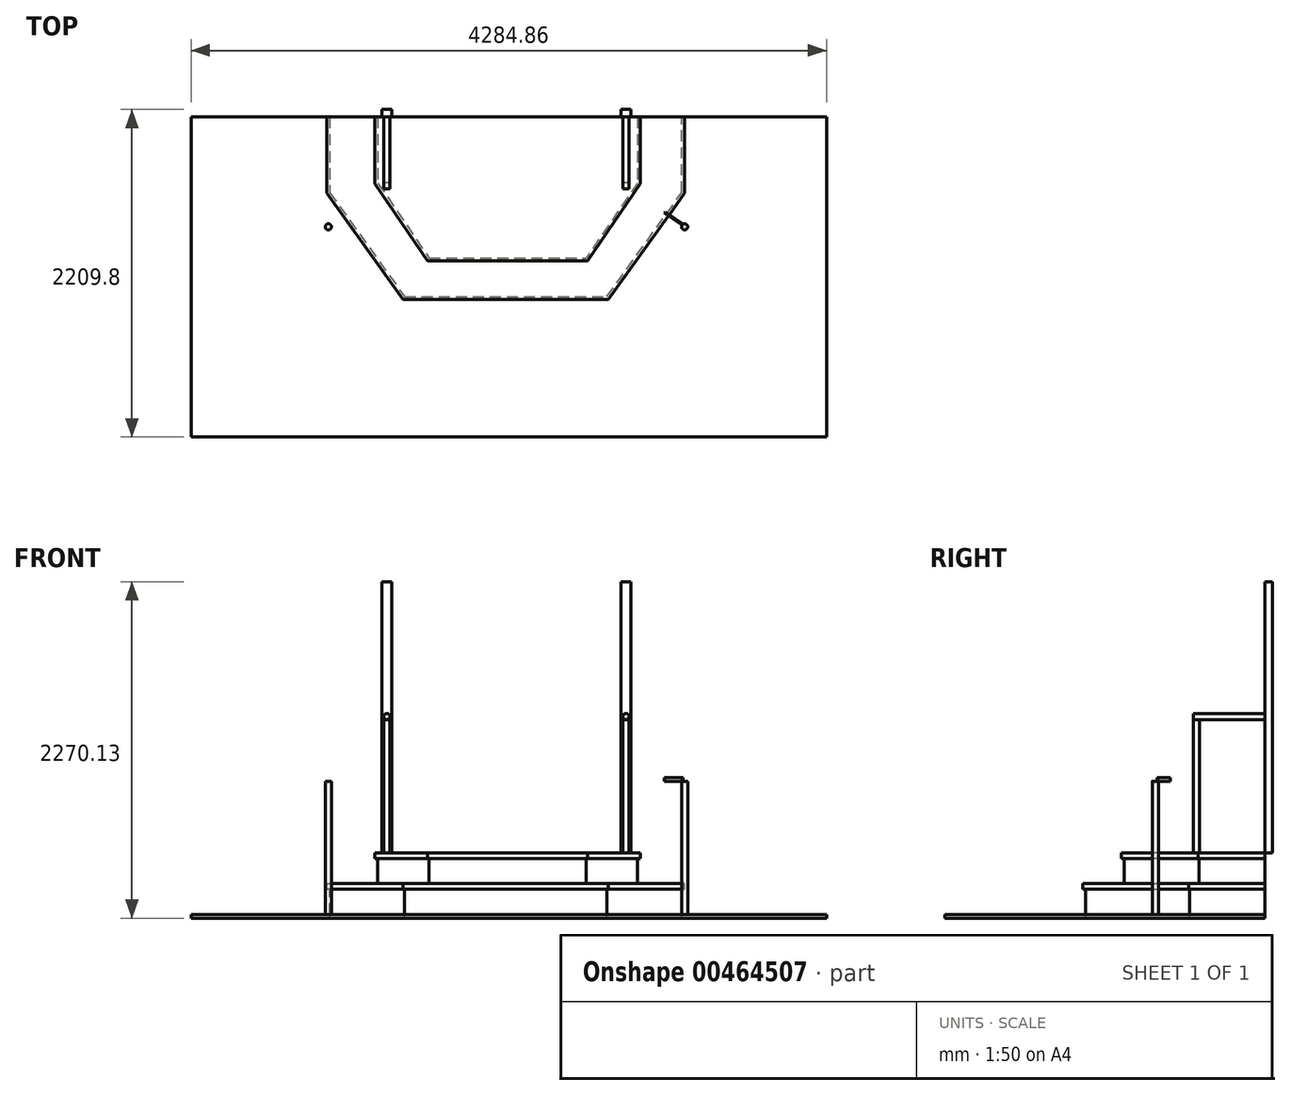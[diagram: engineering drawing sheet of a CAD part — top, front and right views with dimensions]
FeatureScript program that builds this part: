
annotation { "Feature Type Name" : "Feature", "Feature Type Description" : "" }
export const myFeature = defineFeature(function(context is Context, id is Id, definition is map)
    precondition{}
    {
        {
            var Q0;
            Q0=qCreatedBy(makeId("Top.planeOp"),FACE);
            var sketch = newSketch(context, id + "F0", { "sketchPlane" : qUnion([Q0])});
            skLineSegment(sketch, "E0", {"start": v(0, 0) * mm, "end": v(-895.35, 0) * mm});
            skLineSegment(sketch, "E1", {"start": v(-895.35, 0) * mm, "end": v(-895.35, -450.85) * mm});
            skLineSegment(sketch, "E2", {"start": v(-895.35, -450.85) * mm, "end": v(-539.75, -969.26) * mm});
            skLineSegment(sketch, "E3", {"start": v(-539.75, -969.26) * mm, "end": v(0, -969.26) * mm});
            skLineSegment(sketch, "E4", {"start": v(0, -969.26) * mm, "end": v(0, 0) * mm});
            skLineSegment(sketch, "E5.MirrorCS", {"start": v(0, 0) * mm, "end": v(895.35, 0) * mm});
            skLineSegment(sketch, "E6.MirrorCS", {"start": v(895.35, 0) * mm, "end": v(895.35, -450.85) * mm});
            skLineSegment(sketch, "E7.MirrorCS", {"start": v(895.35, -450.85) * mm, "end": v(539.75, -969.26) * mm});
            skLineSegment(sketch, "E8.MirrorCS", {"start": v(539.75, -969.26) * mm, "end": v(0, -969.26) * mm});
            skSolve(sketch);
        }
        {
            var Q0;
            Q0=makeQuery(id+"F0.imprint","IMPRINT",FACE,{"disambiguationData":[TD([[makeQuery(id+"F0.imprint","IMPRINT",EDGE,{"derivedFrom":sQuery(id+"F0.wireOp",EDGE,"E0")}),1.0]])]});
            var Q1;
            Q1=makeQuery(id+"F0.imprint","IMPRINT",FACE,{"disambiguationData":[TD([[makeQuery(id+"F0.imprint","IMPRINT",EDGE,{"derivedFrom":sQuery(id+"F0.wireOp",EDGE,"E4")}),-1.0]])]});
            extrude(context, id + "F1", {"entities" : qUnion([Q0, Q1]), "oppositeDirection" : true, "depth" : 38.1 * mm});
        }
        {
            var Q0;
            Q0=makeQuery(id+"F1.opExtrude","CAP_FACE",FACE,{"disambiguationData":[OSD([sQuery(id+"F0.wireOp",EDGE,"E0"),sQuery(id+"F0.wireOp",EDGE,"E1"),sQuery(id+"F0.wireOp",EDGE,"E2"),sQuery(id+"F0.wireOp",EDGE,"E3"),sQuery(id+"F0.wireOp",EDGE,"E5.MirrorCS"),sQuery(id+"F0.wireOp",EDGE,"E6.MirrorCS"),sQuery(id+"F0.wireOp",EDGE,"E7.MirrorCS"),sQuery(id+"F0.wireOp",EDGE,"E8.MirrorCS")])],"isStart":false});
            var sketch = newSketch(context, id + "F2", { "sketchPlane" : qUnion([Q0])});
            skLineSegment(sketch, "E9.0", {"start": v(876.3, 0) * mm, "end": v(876.3, 444.94) * mm});
            skLineSegment(sketch, "E9.1", {"start": v(-876.3, 0) * mm, "end": v(-876.3, 444.94) * mm});
            skLineSegment(sketch, "E9.2", {"start": v(-876.3, 444.94) * mm, "end": v(-529.72, 950.21) * mm});
            skLineSegment(sketch, "E9.3", {"start": v(-529.72, 950.21) * mm, "end": v(529.72, 950.21) * mm});
            skLineSegment(sketch, "E9.4", {"start": v(876.3, 444.94) * mm, "end": v(529.72, 950.21) * mm});
            skSolve(sketch);
        }
        {
            var Q0;
            {var subQ1=sQuery(id+"F2.wireOp",EDGE,"E9.0");Q0=makeQuery(id+"F2.imprint","IMPRINT",FACE,{"disambiguationData":[TD([[makeQuery(id+"F2.imprint","IMPRINT",EDGE,{"derivedFrom":subQ1}),1.0]])]});}
            extrude(context, id + "F3", {"entities" : qUnion([Q0]), "operationType" : NewBodyOperationType.ADD, "depth" : 168.27 * mm});
        }
        {
            var Q0;
            Q0=makeQuery(id+"F3.opExtrude","CAP_FACE",FACE,{"disambiguationData":[OSD([sQuery(id+"F0.wireOp",EDGE,"E0"),sQuery(id+"F0.wireOp",EDGE,"E5.MirrorCS"),sQuery(id+"F2.wireOp",EDGE,"E9.0"),sQuery(id+"F2.wireOp",EDGE,"E9.1"),sQuery(id+"F2.wireOp",EDGE,"E9.2"),sQuery(id+"F2.wireOp",EDGE,"E9.3"),sQuery(id+"F2.wireOp",EDGE,"E9.4")])],"isStart":false});
            var sketch = newSketch(context, id + "F4", { "sketchPlane" : qUnion([Q0])});
            skLineSegment(sketch, "E10", {"start": v(0, 0) * mm, "end": v(-1219.2, 0) * mm});
            skLineSegment(sketch, "E11", {"start": v(0, 0) * mm, "end": v(1193.8, 0) * mm});
            skLineSegment(sketch, "E12", {"start": v(-1219.2, 0) * mm, "end": v(-1219.2, 514.35) * mm});
            skLineSegment(sketch, "E13", {"start": v(-1219.2, 514.35) * mm, "end": v(-704.85, 1231.65) * mm});
            skLineSegment(sketch, "E14", {"start": v(-704.85, 1231.65) * mm, "end": v(679.45, 1231.65) * mm});
            skLineSegment(sketch, "E15", {"start": v(679.45, 1231.65) * mm, "end": v(1193.8, 514.35) * mm});
            skLineSegment(sketch, "E16", {"start": v(1193.8, 514.35) * mm, "end": v(1193.8, 0) * mm});
            skSolve(sketch);
        }
        {
            var Q0;
            {var subQ4=sQuery(id+"F4.wireOp",EDGE,"E12");Q0=makeQuery(id+"F4.imprint","IMPRINT",FACE,{"disambiguationData":[TD([[makeQuery(id+"F4.imprint","IMPRINT",EDGE,{"derivedFrom":subQ4}),-1.0]])]});}
            var Q1;
            {var subQ0=makeQuery(id+"F3.opExtrude","CAP_EDGE",EDGE,{"disambiguationData":[OSD([sQuery(id+"F2.wireOp",EDGE,"E9.0")])],"isStart":false});Q1=makeQuery(id+"F4.imprint","IMPRINT",FACE,{"disambiguationData":[TD([[makeQuery(id+"F4.imprint","IMPRINT",EDGE,{"derivedFrom":subQ0}),1.0]])]});}
            extrude(context, id + "F5", {"entities" : qUnion([Q0, Q1]), "operationType" : NewBodyOperationType.ADD, "depth" : 38.1 * mm});
        }
        {
            var Q0;
            Q0=makeQuery(id+"F5.opExtrude","CAP_FACE",FACE,{"disambiguationData":[OSD([sQuery(id+"F4.wireOp",EDGE,"E10"),sQuery(id+"F4.wireOp",EDGE,"E11"),sQuery(id+"F4.wireOp",EDGE,"E12"),sQuery(id+"F4.wireOp",EDGE,"E13"),sQuery(id+"F4.wireOp",EDGE,"E14"),sQuery(id+"F4.wireOp",EDGE,"E15"),sQuery(id+"F4.wireOp",EDGE,"E16")])],"isStart":false});
            var sketch = newSketch(context, id + "F6", { "sketchPlane" : qUnion([Q0])});
            skLineSegment(sketch, "E17.0", {"start": v(1174.75, 508.23) * mm, "end": v(1174.75, 0) * mm});
            skLineSegment(sketch, "E17.1", {"start": v(-1200.15, 0) * mm, "end": v(-1200.15, 508.23) * mm});
            skLineSegment(sketch, "E17.2", {"start": v(-1200.15, 508.23) * mm, "end": v(-695.07, 1212.6) * mm});
            skLineSegment(sketch, "E17.3", {"start": v(-695.07, 1212.6) * mm, "end": v(669.67, 1212.6) * mm});
            skLineSegment(sketch, "E17.4", {"start": v(669.67, 1212.6) * mm, "end": v(1174.75, 508.23) * mm});
            skSolve(sketch);
        }
        {
            var Q0;
            {var subQ1=sQuery(id+"F6.wireOp",EDGE,"E17.0");Q0=makeQuery(id+"F6.imprint","IMPRINT",FACE,{"disambiguationData":[TD([[makeQuery(id+"F6.imprint","IMPRINT",EDGE,{"derivedFrom":subQ1}),-1.0]])]});}
            extrude(context, id + "F7", {"entities" : qUnion([Q0]), "operationType" : NewBodyOperationType.ADD, "depth" : 171.45 * mm});
        }
        {
            var Q0;
            Q0=makeQuery(id+"F7.opExtrude","CAP_FACE",FACE,{"disambiguationData":[OSD([sQuery(id+"F4.wireOp",EDGE,"E10"),sQuery(id+"F4.wireOp",EDGE,"E11"),sQuery(id+"F6.wireOp",EDGE,"E17.0"),sQuery(id+"F6.wireOp",EDGE,"E17.1"),sQuery(id+"F6.wireOp",EDGE,"E17.2"),sQuery(id+"F6.wireOp",EDGE,"E17.3"),sQuery(id+"F6.wireOp",EDGE,"E17.4")])],"isStart":false});
            var sketch = newSketch(context, id + "F8", { "sketchPlane" : qUnion([Q0])});
            skLineSegment(sketch, "E18.bottom", {"start": v(0, 0) * mm, "end": v(-2134.43, 0) * mm});
            skLineSegment(sketch, "E18.top", {"start": v(0, 2159) * mm, "end": v(-2134.43, 2159) * mm});
            skLineSegment(sketch, "E18.left", {"start": v(0, 0) * mm, "end": v(0, 2159) * mm});
            skLineSegment(sketch, "E18.right", {"start": v(-2134.43, 0) * mm, "end": v(-2134.43, 2159) * mm});
            skLineSegment(sketch, "E19.bottom", {"start": v(0, 0) * mm, "end": v(2150.43, 0) * mm});
            skLineSegment(sketch, "E19.top", {"start": v(0, 2159) * mm, "end": v(2150.43, 2159) * mm});
            skLineSegment(sketch, "E19.right", {"start": v(2150.43, 0) * mm, "end": v(2150.43, 2159) * mm});
            skSolve(sketch);
        }
        {
            var Q0;
            {var subQ1=sQuery(id+"F8.wireOp",EDGE,"E18.top");Q0=makeQuery(id+"F8.imprint","IMPRINT",FACE,{"disambiguationData":[TD([[makeQuery(id+"F8.imprint","IMPRINT",EDGE,{"derivedFrom":subQ1}),1.0]])]});}
            var Q1;
            {var subQ2=sQuery(id+"F8.wireOp",EDGE,"E19.top");Q1=makeQuery(id+"F8.imprint","IMPRINT",FACE,{"disambiguationData":[TD([[makeQuery(id+"F8.imprint","IMPRINT",EDGE,{"derivedFrom":subQ2}),-1.0]])]});}
            extrude(context, id + "F9", {"entities" : qUnion([Q0, Q1]), "depth" : 25.4 * mm});
        }
        {
            var Q0;
            {var subQ0=sQuery(id+"F4.wireOp",EDGE,"E11");var subQ1=sQuery(id+"F4.wireOp",EDGE,"E10");var subQ2=sQuery(id+"F0.wireOp",EDGE,"E5.MirrorCS");var subQ3=sQuery(id+"F0.wireOp",EDGE,"E0");Q0=makeQuery(id+"F7.boolean.opBoolean","MERGE",FACE,{"derivedFrom":[makeQuery(id+"F5.boolean.opBoolean","MERGE",FACE,{"derivedFrom":[makeQuery(id+"F3.boolean.opBoolean","MERGE",FACE,{"derivedFrom":[makeQuery(id+"F1.opExtrude","SWEPT_FACE",FACE,{"disambiguationData":[OSD([subQ3,subQ2])]}),makeQuery(id+"F3.opExtrude","SWEPT_FACE",FACE,{"disambiguationData":[OSD([subQ3,subQ2])]})]}),makeQuery(id+"F5.opExtrude","SWEPT_FACE",FACE,{"disambiguationData":[OSD([subQ1,subQ0])]})]}),makeQuery(id+"F7.opExtrude","SWEPT_FACE",FACE,{"disambiguationData":[OSD([subQ1,subQ0])]})]});}
            var sketch = newSketch(context, id + "F10", { "sketchPlane" : qUnion([Q0])});
            skLineSegment(sketch, "E20.bottom", {"start": v(847.72, 0) * mm, "end": v(781.05, 0) * mm});
            skLineSegment(sketch, "E20.top", {"start": v(847.72, 1828.8) * mm, "end": v(781.05, 1828.8) * mm});
            skLineSegment(sketch, "E20.left", {"start": v(847.72, 0) * mm, "end": v(847.72, 1828.8) * mm});
            skLineSegment(sketch, "E20.right", {"start": v(781.05, 0) * mm, "end": v(781.05, 1828.8) * mm});
            skLineSegment(sketch, "E21.bottom", {"start": v(-765.17, 0) * mm, "end": v(-831.85, 0) * mm});
            skLineSegment(sketch, "E21.top", {"start": v(-765.17, 1828.8) * mm, "end": v(-831.85, 1828.8) * mm});
            skLineSegment(sketch, "E21.left", {"start": v(-765.17, 0) * mm, "end": v(-765.17, 1828.8) * mm});
            skLineSegment(sketch, "E21.right", {"start": v(-831.85, 0) * mm, "end": v(-831.85, 1828.8) * mm});
            skSolve(sketch);
        }
        {
            var Q0;
            Q0=makeQuery(id+"F10.imprint","IMPRINT",FACE,{"disambiguationData":[TD([[makeQuery(id+"F10.imprint","IMPRINT",EDGE,{"derivedFrom":sQuery(id+"F10.wireOp",EDGE,"E20.bottom")}),1.0]])]});
            var Q1;
            Q1=makeQuery(id+"F10.imprint","IMPRINT",FACE,{"disambiguationData":[TD([[makeQuery(id+"F10.imprint","IMPRINT",EDGE,{"derivedFrom":sQuery(id+"F10.wireOp",EDGE,"E21.bottom")}),1.0]])]});
            extrude(context, id + "F11", {"entities" : qUnion([Q0, Q1]), "depth" : 50.8 * mm});
        }
        {
            var Q0;
            Q0=makeQuery(id+"F1.opExtrude","CAP_FACE",FACE,{"disambiguationData":[OSD([sQuery(id+"F0.wireOp",EDGE,"E0"),sQuery(id+"F0.wireOp",EDGE,"E1"),sQuery(id+"F0.wireOp",EDGE,"E2"),sQuery(id+"F0.wireOp",EDGE,"E3"),sQuery(id+"F0.wireOp",EDGE,"E5.MirrorCS"),sQuery(id+"F0.wireOp",EDGE,"E6.MirrorCS"),sQuery(id+"F0.wireOp",EDGE,"E7.MirrorCS"),sQuery(id+"F0.wireOp",EDGE,"E8.MirrorCS")])],"isStart":true});
            var sketch = newSketch(context, id + "F12", { "sketchPlane" : qUnion([Q0])});
            skPoint(sketch, "E22.0", {"position": v(831.85, 0) * mm});
            skPoint(sketch, "E23.0", {"position": v(765.17, 0) * mm});
            skPoint(sketch, "E24.0", {"position": v(-847.72, 0) * mm});
            skPoint(sketch, "E25.0", {"position": v(-781.05, 0) * mm});
            skCircle(sketch, "E26", {"center": v(798.51, -463.55) * mm, "radius": 20.64 * mm});
            skLineSegment(sketch, "E27", {"start": v(798.51, 0) * mm, "end": v(798.51, -463.55) * mm});
            skLineSegment(sketch, "E28", {"start": v(798.51, -463.55) * mm, "end": v(1218.12, -751.38) * mm});
            skCircle(sketch, "E29", {"center": v(-814.37, -463.55) * mm, "radius": 20.64 * mm});
            skSolve(sketch);
        }
        {
            var Q0;
            {var subQ0=sQuery(id+"F12.wireOp",EDGE,"E27");var subQ1=sQuery(id+"F12.wireOp",EDGE,"E26");var subQ2=makeQuery(id+"F12.imprint","INTERSECT",VERTEX,{"derivedFrom":[subQ1,subQ0]});Q0=makeQuery(id+"F12.imprint","IMPRINT",FACE,{"disambiguationData":[TD([[makeQuery(id+"F12.imprint","IMPRINT",EDGE,{"disambiguationData":[TD([[subQ2,-1.0]])],"derivedFrom":subQ1}),1.0]])]});}
            var Q1;
            {var subQ0=sQuery(id+"F12.wireOp",EDGE,"E27");var subQ1=sQuery(id+"F12.wireOp",EDGE,"E26");var subQ2=makeQuery(id+"F12.imprint","INTERSECT",VERTEX,{"derivedFrom":[subQ1,subQ0]});Q1=makeQuery(id+"F12.imprint","IMPRINT",FACE,{"disambiguationData":[TD([[makeQuery(id+"F12.imprint","IMPRINT",EDGE,{"disambiguationData":[TD([[subQ2,1.0]])],"derivedFrom":subQ1}),1.0]])]});}
            var Q2;
            Q2=makeQuery(id+"F12.imprint","IMPRINT",FACE,{"disambiguationData":[TD([[makeQuery(id+"F12.imprint","IMPRINT",EDGE,{"derivedFrom":sQuery(id+"F12.wireOp",EDGE,"E29")}),1.0]])]});
            extrude(context, id + "F13", {"entities" : qUnion([Q0, Q1, Q2]), "operationType" : NewBodyOperationType.ADD, "depth" : 898.52 * mm});
        }
        {
            var Q0;
            Q0=makeQuery(id+"F11.opExtrude","CAP_FACE",FACE,{"disambiguationData":[OSD([sQuery(id+"F10.wireOp",EDGE,"E21.bottom"),sQuery(id+"F10.wireOp",EDGE,"E21.top"),sQuery(id+"F10.wireOp",EDGE,"E21.left"),sQuery(id+"F10.wireOp",EDGE,"E21.right")])],"isStart":true});
            var sketch = newSketch(context, id + "F14", { "sketchPlane" : qUnion([Q0])});
            skCircle(sketch, "E30", {"center": v(798.51, 919.16) * mm, "radius": 20.64 * mm});
            skSolve(sketch);
        }
        {
            var Q0;
            {var subQ0=sQuery(id+"F4.wireOp",EDGE,"E11");var subQ1=sQuery(id+"F4.wireOp",EDGE,"E10");var subQ2=sQuery(id+"F0.wireOp",EDGE,"E5.MirrorCS");var subQ3=sQuery(id+"F0.wireOp",EDGE,"E0");Q0=makeQuery(id+"F7.boolean.opBoolean","MERGE",FACE,{"derivedFrom":[makeQuery(id+"F5.boolean.opBoolean","MERGE",FACE,{"derivedFrom":[makeQuery(id+"F3.boolean.opBoolean","MERGE",FACE,{"derivedFrom":[makeQuery(id+"F1.opExtrude","SWEPT_FACE",FACE,{"disambiguationData":[OSD([subQ3,subQ2])]}),makeQuery(id+"F3.opExtrude","SWEPT_FACE",FACE,{"disambiguationData":[OSD([subQ3,subQ2])]})]}),makeQuery(id+"F5.opExtrude","SWEPT_FACE",FACE,{"disambiguationData":[OSD([subQ1,subQ0])]})]}),makeQuery(id+"F7.opExtrude","SWEPT_FACE",FACE,{"disambiguationData":[OSD([subQ1,subQ0])]})]});}
            var sketch = newSketch(context, id + "F15", { "sketchPlane" : qUnion([Q0])});
            skLineSegment(sketch, "E31", {"start": v(-895.35, 0) * mm, "end": v(-1518, -430.56) * mm});
            skSolve(sketch);
        }
        {
            var Q0;
            Q0=makeQuery(id+"F1.opExtrude","CAP_FACE",FACE,{"disambiguationData":[OSD([sQuery(id+"F0.wireOp",EDGE,"E0"),sQuery(id+"F0.wireOp",EDGE,"E1"),sQuery(id+"F0.wireOp",EDGE,"E2"),sQuery(id+"F0.wireOp",EDGE,"E3"),sQuery(id+"F0.wireOp",EDGE,"E5.MirrorCS"),sQuery(id+"F0.wireOp",EDGE,"E6.MirrorCS"),sQuery(id+"F0.wireOp",EDGE,"E7.MirrorCS"),sQuery(id+"F0.wireOp",EDGE,"E8.MirrorCS")])],"isStart":true});
            cPlane(context, id + "F16", {"entities" : qUnion([Q0]), "cplaneType" : CPlaneType.OFFSET, "offset" : 939.8 * mm, "width" : 152.4 * mm, "height" : 152.4 * mm});
        }
        {
            var Q0;
            Q0=qCreatedBy(id+"F16.planeOp",FACE);
            var sketch = newSketch(context, id + "F17", { "sketchPlane" : qUnion([Q0])});
            skLineSegment(sketch, "E32.0", {"start": v(819.15, -484.19) * mm, "end": v(777.88, -484.19) * mm});
            skLineSegment(sketch, "E33", {"start": v(819.15, 0) * mm, "end": v(819.15, -484.19) * mm});
            skLineSegment(sketch, "E34", {"start": v(777.88, -484.19) * mm, "end": v(819.15, -425.24) * mm});
            skLineSegment(sketch, "E35.0", {"start": v(895.35, -450.85) * mm, "end": v(539.75, -969.26) * mm});
            skLineSegment(sketch, "E35.1", {"start": v(895.35, 0) * mm, "end": v(895.35, -450.85) * mm});
            skSolve(sketch);
        }
        {
            var Q0;
            Q0=makeQuery(id+"F9.opExtrude","CAP_FACE",FACE,{"disambiguationData":[OSD([sQuery(id+"F6.wireOp",EDGE,"E17.0"),sQuery(id+"F6.wireOp",EDGE,"E17.1"),sQuery(id+"F6.wireOp",EDGE,"E17.2"),sQuery(id+"F6.wireOp",EDGE,"E17.3"),sQuery(id+"F6.wireOp",EDGE,"E17.4"),sQuery(id+"F8.wireOp",EDGE,"E18.bottom"),sQuery(id+"F8.wireOp",EDGE,"E18.top"),sQuery(id+"F8.wireOp",EDGE,"E18.right"),sQuery(id+"F8.wireOp",EDGE,"E19.bottom"),sQuery(id+"F8.wireOp",EDGE,"E19.top"),sQuery(id+"F8.wireOp",EDGE,"E19.right")])],"isStart":true});
            var sketch = newSketch(context, id + "F18", { "sketchPlane" : qUnion([Q0])});
            skLineSegment(sketch, "E36", {"start": v(819.15, 0) * mm, "end": v(819.15, -425.24) * mm});
            skLineSegment(sketch, "E37.0", {"start": v(777.88, -484.19) * mm, "end": v(819.15, -425.24) * mm});
            skCircle(sketch, "E38.0", {"center": v(798.51, -463.55) * mm, "radius": 20.64 * mm});
            skLineSegment(sketch, "E39.0", {"start": v(1193.8, -514.35) * mm, "end": v(1193.8, 0) * mm});
            skLineSegment(sketch, "E40.0", {"start": v(679.45, -1231.65) * mm, "end": v(1193.8, -514.35) * mm});
            skLineSegment(sketch, "E41.0", {"start": v(895.35, 0) * mm, "end": v(895.35, -450.85) * mm});
            skLineSegment(sketch, "E42.0", {"start": v(895.35, -450.85) * mm, "end": v(539.75, -969.26) * mm});
            skLineSegment(sketch, "E43", {"start": v(798.51, -463.55) * mm, "end": v(1569.43, -1003.35) * mm});
            skLineSegment(sketch, "E44", {"start": v(1193.8, -514.35) * mm, "end": v(1193.8, -773.1) * mm});
            skCircle(sketch, "E45", {"center": v(1193.8, -740.33) * mm, "radius": 20.64 * mm});
            skCircle(sketch, "E46", {"center": v(-1209.67, -740.33) * mm, "radius": 20.64 * mm});
            skCircle(sketch, "E47.0", {"center": v(-814.37, -463.55) * mm, "radius": 20.64 * mm});
            skSolve(sketch);
        }
        {
            var Q0;
            {var subQ0=sQuery(id+"F18.wireOp",EDGE,"E45");var subQ1=sQuery(id+"F18.wireOp",EDGE,"E43");var subQ2=makeQuery(id+"F18.imprint","INTERSECT",VERTEX,{"disambiguationData":[OD(0.0)],"derivedFrom":[subQ1,subQ0]});Q0=makeQuery(id+"F18.imprint","IMPRINT",FACE,{"disambiguationData":[TD([[makeQuery(id+"F18.imprint","IMPRINT",EDGE,{"disambiguationData":[TD([[subQ2,1.0]])],"derivedFrom":subQ1}),1.0]])]});}
            var Q1;
            {var subQ0=sQuery(id+"F18.wireOp",EDGE,"E45");var subQ1=sQuery(id+"F18.wireOp",EDGE,"E43");var subQ2=makeQuery(id+"F18.imprint","INTERSECT",VERTEX,{"disambiguationData":[OD(1.0)],"derivedFrom":[subQ1,subQ0]});Q1=makeQuery(id+"F18.imprint","IMPRINT",FACE,{"disambiguationData":[TD([[makeQuery(id+"F18.imprint","IMPRINT",EDGE,{"disambiguationData":[TD([[subQ2,-1.0]])],"derivedFrom":subQ1}),1.0]])]});}
            var Q2;
            {var subQ0=sQuery(id+"F18.wireOp",EDGE,"E45");var subQ1=sQuery(id+"F18.wireOp",EDGE,"E43");var subQ2=makeQuery(id+"F18.imprint","INTERSECT",VERTEX,{"disambiguationData":[OD(1.0)],"derivedFrom":[subQ1,subQ0]});Q2=makeQuery(id+"F18.imprint","IMPRINT",FACE,{"disambiguationData":[TD([[makeQuery(id+"F18.imprint","IMPRINT",EDGE,{"disambiguationData":[TD([[subQ2,-1.0]])],"derivedFrom":subQ1}),-1.0]])]});}
            var Q3;
            {var subQ0=sQuery(id+"F18.wireOp",EDGE,"E45");var subQ1=sQuery(id+"F18.wireOp",EDGE,"E43");var subQ2=makeQuery(id+"F18.imprint","INTERSECT",VERTEX,{"disambiguationData":[OD(0.0)],"derivedFrom":[subQ1,subQ0]});Q3=makeQuery(id+"F18.imprint","IMPRINT",FACE,{"disambiguationData":[TD([[makeQuery(id+"F18.imprint","IMPRINT",EDGE,{"disambiguationData":[TD([[subQ2,1.0]])],"derivedFrom":subQ1}),-1.0]])]});}
            var Q4;
            Q4=makeQuery(id+"F18.imprint","IMPRINT",FACE,{"disambiguationData":[TD([[makeQuery(id+"F18.imprint","IMPRINT",EDGE,{"derivedFrom":sQuery(id+"F18.wireOp",EDGE,"E46")}),1.0]])]});
            extrude(context, id + "F19", {"entities" : qUnion([Q0, Q1, Q2, Q3, Q4]), "operationType" : NewBodyOperationType.ADD, "depth" : 898.52 * mm});
        }
        {
            var Q0;
            Q0=makeQuery(id+"F14.imprint","IMPRINT",FACE,{"disambiguationData":[TD([[makeQuery(id+"F14.imprint","IMPRINT",EDGE,{"derivedFrom":sQuery(id+"F14.wireOp",EDGE,"E30")}),1.0]])]});
            extrude(context, id + "F20", {"entities" : qUnion([Q0]), "depth" : 484.17 * mm});
        }
        {
            var Q0;
            Q0=makeQuery(id+"F14.imprint","IMPRINT",FACE,{"disambiguationData":[TD([[makeQuery(id+"F14.imprint","IMPRINT",EDGE,{"derivedFrom":sQuery(id+"F14.wireOp",EDGE,"E30")}),-1.0]])]});
            var sketch = newSketch(context, id + "F21", { "sketchPlane" : qUnion([Q0])});
            skCircle(sketch, "E48", {"center": v(798.51, 614.36) * mm, "radius": 19.05 * mm});
            skCircle(sketch, "E49", {"center": v(798.51, 309.56) * mm, "radius": 19.05 * mm});
            skLineSegment(sketch, "E50.0", {"start": v(-847.72, 0) * mm, "end": v(-847.72, 1828.8) * mm});
            skLineSegment(sketch, "E51.0", {"start": v(-781.05, 0) * mm, "end": v(-781.05, 1828.8) * mm});
            skCircle(sketch, "E52", {"center": v(-814.39, 309.56) * mm, "radius": 9.53 * mm});
            skCircle(sketch, "E53", {"center": v(-814.39, 614.36) * mm, "radius": 12.7 * mm});
            skCircle(sketch, "E54", {"center": v(-814.39, 919.16) * mm, "radius": 20.64 * mm});
            skSolve(sketch);
        }
        {
            var Q0;
            Q0=sQuery(id+"F21.wireOp",EDGE,"E48");
            var Q1;
            Q1=sQuery(id+"F21.wireOp",EDGE,"E49");
            var Q2;
            Q2=sQuery(id+"F21.wireOp",EDGE,"E52");
            var Q3;
            Q3=sQuery(id+"F21.wireOp",EDGE,"E53");
            extrude(context, id + "F22", {"bodyType" : ToolBodyType.SURFACE, "surfaceEntities" : qUnion([Q0, Q1, Q2, Q3]), "endBound" : BoundingType.UP_TO_NEXT, "depth" : 25.4 * mm});
        }
        {
            var Q0;
            Q0=makeQuery(id+"F21.imprint","IMPRINT",FACE,{"disambiguationData":[TD([[makeQuery(id+"F21.imprint","IMPRINT",EDGE,{"derivedFrom":sQuery(id+"F21.wireOp",EDGE,"E54")}),1.0]])]});
            extrude(context, id + "F23", {"entities" : qUnion([Q0]), "depth" : 484.17 * mm});
        }
        {
            var Q0;
            Q0=makeQuery(id+"F19.opExtrude","CAP_FACE",FACE,{"disambiguationData":[OSD([sQuery(id+"F18.wireOp",EDGE,"E45")])],"isStart":false});
            var sketch = newSketch(context, id + "F24", { "sketchPlane" : qUnion([Q0])});
            skCircle(sketch, "E55.0", {"center": v(798.51, -463.55) * mm, "radius": 20.64 * mm});
            skLineSegment(sketch, "E56", {"start": v(798.51, -463.55) * mm, "end": v(1193.8, -740.33) * mm});
            skLineSegment(sketch, "E57", {"start": v(1193.8, -740.33) * mm, "end": v(1197.94, -734.42) * mm});
            skLineSegment(sketch, "E58", {"start": v(1197.94, -734.42) * mm, "end": v(798.51, -454.73) * mm});
            skLineSegment(sketch, "E59", {"start": v(798.51, -454.73) * mm, "end": v(798.51, -463.55) * mm});
            skLineSegment(sketch, "E60", {"start": v(1061.45, -638.85) * mm, "end": v(1057.3, -644.76) * mm});
            skSolve(sketch);
        }
        {
            var Q0;
            {var subQ0=sQuery(id+"F24.wireOp",EDGE,"E60");Q0=makeQuery(id+"F24.imprint","IMPRINT",FACE,{"disambiguationData":[TD([[makeQuery(id+"F24.imprint","IMPRINT",EDGE,{"derivedFrom":subQ0}),1.0]])]});}
            extrude(context, id + "F25", {"entities" : qUnion([Q0]), "depth" : 25.4 * mm, "offsetDistance" : 25.4 * mm});
        }
    });
